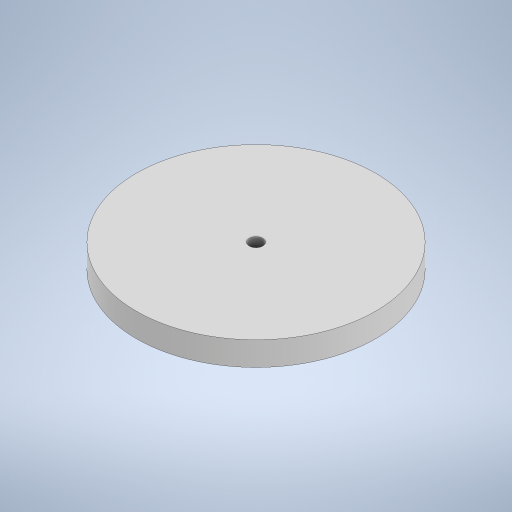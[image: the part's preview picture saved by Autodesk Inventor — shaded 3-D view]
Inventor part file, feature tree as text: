
AUTODESK INVENTOR PART (.ipt)
format: ipt  version: 2023 (Build 270158030, 158C)  size: 231,424 bytes
history: native  units: in
note: dims shown in document units (in); Inventor stores cm internally (conversion verified against a paired STEP export)
features: sketch x3, extrude x2, hole x1, chamfer x1
ambient origin geometry x8: Origin, YZ Plane, XZ Plane, XY Plane, X Axis, Y Axis, Z Axis, Center Point
bodies: Solid1 (feature_tree)
feature tree (7):
  extrude  "Extrusion1"  Depth=0.5in TaperAngle=0.0deg
  hole  "Hole1"  [1 undecoded]
  extrude  "Extrusion2"  Depth=0.172in TaperAngle=45.0deg
  chamfer  "Chamfer1"  [1 undecoded]
  sketch  "Sketch1"  dims[d0=5.0in d1=0.5in d2=0.0in]
  sketch  "Sketch2"  dims[d3=0.281in d4=0.75in d5=0.75in d6=0.188in d7=0.5635in d8=1.0in d9=0.8108in d10=0.438in]
  sketch  "Sketch3"  dims[d11=0.172in d12=0.0in d13=0.02in d14=0.125in d15=45.0deg]
note: 2 required parameter values undecoded (feature->parameter linkage not recoverable at this tier; creation-order binding heuristic only, values carry confidence <= 0.55)
